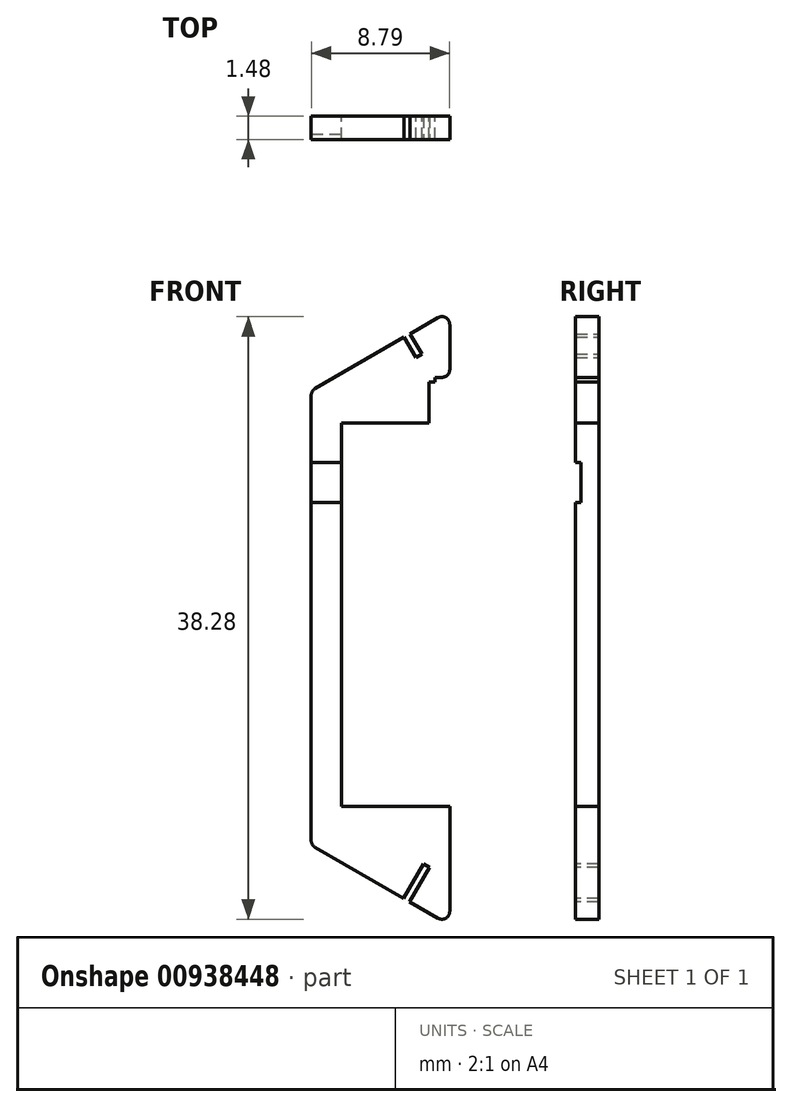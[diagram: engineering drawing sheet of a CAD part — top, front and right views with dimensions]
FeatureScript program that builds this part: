
annotation { "Feature Type Name" : "Feature", "Feature Type Description" : "" }
export const myFeature = defineFeature(function(context is Context, id is Id, definition is map)
    precondition{}
    {
        {
            var Q0;
            Q0=qCreatedBy(makeId("Front.planeOp"),FACE);
            var sketch = newSketch(context, id + "F0", { "sketchPlane" : qUnion([Q0])});
            skLineSegment(sketch, "E0", {"start": v(7.5, 30.48) * mm, "end": v(-1.3, 25.4) * mm});
            skLineSegment(sketch, "E1", {"start": v(-1.3, 25.4) * mm, "end": v(-1.3, -3.45) * mm});
            skLineSegment(sketch, "E2", {"start": v(-1.3, -3.45) * mm, "end": v(7.5, -8.53) * mm});
            skLineSegment(sketch, "E3", {"start": v(7.5, 30.48) * mm, "end": v(7.5, -8.53) * mm});
            skSolve(sketch);
        }
        {
            var Q0;
            Q0=makeQuery(id+"F0.imprint","IMPRINT",FACE,{"disambiguationData":[TD([[makeQuery(id+"F0.imprint","IMPRINT",EDGE,{"derivedFrom":sQuery(id+"F0.wireOp",EDGE,"E0")}),1.0]])]});
            extrude(context, id + "F1", {"entities" : qUnion([Q0]), "depth" : 16.18 * mm, "offsetDistance" : 25.4 * mm});
        }
        {
            var Q0;
            Q0=makeQuery(id+"F1.opExtrude","SWEPT_FACE",FACE,{"disambiguationData":[OSD([sQuery(id+"F0.wireOp",EDGE,"E3")])]});
            var sketch = newSketch(context, id + "F2", { "sketchPlane" : qUnion([Q0])});
            skLineSegment(sketch, "E4.bottom", {"start": v(-1.48, -8.53) * mm, "end": v(-16.18, -8.53) * mm});
            skLineSegment(sketch, "E4.top", {"start": v(-1.48, 30.48) * mm, "end": v(-16.18, 30.48) * mm});
            skLineSegment(sketch, "E4.left", {"start": v(-1.48, -8.53) * mm, "end": v(-1.48, 30.48) * mm});
            skLineSegment(sketch, "E4.right", {"start": v(-16.18, -8.53) * mm, "end": v(-16.18, 30.48) * mm});
            skSolve(sketch);
        }
        {
            var Q0;
            Q0=makeQuery(id+"F2.imprint","IMPRINT",FACE,{"disambiguationData":[TD([[makeQuery(id+"F2.imprint","IMPRINT",EDGE,{"derivedFrom":sQuery(id+"F2.wireOp",EDGE,"E4.bottom")}),1.0]])]});
            extrude(context, id + "F3", {"entities" : qUnion([Q0]), "operationType" : NewBodyOperationType.REMOVE, "oppositeDirection" : true, "depth" : 25.4 * mm, "offsetDistance" : 25.4 * mm});
        }
        {
            var Q0;
            Q0=makeQuery(id+"F0.imprint","IMPRINT",FACE,{"disambiguationData":[TD([[makeQuery(id+"F0.imprint","IMPRINT",EDGE,{"derivedFrom":sQuery(id+"F0.wireOp",EDGE,"E0")}),1.0]])]});
            var sketch = newSketch(context, id + "F4", { "sketchPlane" : qUnion([Q0])});
            skLineSegment(sketch, "E5.bottom", {"start": v(7.9, 23.36) * mm, "end": v(0.61, 23.36) * mm});
            skLineSegment(sketch, "E5.top", {"start": v(7.9, -1) * mm, "end": v(0.61, -1) * mm});
            skLineSegment(sketch, "E5.left", {"start": v(7.9, 23.36) * mm, "end": v(7.9, -1) * mm});
            skLineSegment(sketch, "E5.right", {"start": v(0.61, 23.36) * mm, "end": v(0.61, -1) * mm});
            skSolve(sketch);
        }
        {
            var Q0;
            Q0 = qSketchRegion(id + "F4", true);
            extrude(context, id + "F5", {"entities" : qUnion([Q0]), "operationType" : NewBodyOperationType.REMOVE, "depth" : 6.02 * mm, "offsetDistance" : 25.4 * mm});
        }
        {
            var Q0;
            Q0=makeQuery(id+"F1.opExtrude","SWEPT_FACE",FACE,{"disambiguationData":[OSD([sQuery(id+"F0.wireOp",EDGE,"E2")])]});
            var sketch = newSketch(context, id + "F6", { "sketchPlane" : qUnion([Q0])});
            skLineSegment(sketch, "E6.bottom", {"start": v(7.8, 0) * mm, "end": v(7.37, 0) * mm});
            skLineSegment(sketch, "E6.top", {"start": v(7.8, 1.48) * mm, "end": v(7.37, 1.48) * mm});
            skLineSegment(sketch, "E6.left", {"start": v(7.8, 0) * mm, "end": v(7.8, 1.48) * mm});
            skLineSegment(sketch, "E6.right", {"start": v(7.37, 0) * mm, "end": v(7.37, 1.48) * mm});
            skSolve(sketch);
        }
        {
            var Q0;
            Q0=makeQuery(id+"F6.imprint","IMPRINT",FACE,{"disambiguationData":[TD([[makeQuery(id+"F6.imprint","IMPRINT",EDGE,{"derivedFrom":sQuery(id+"F6.wireOp",EDGE,"E6.bottom")}),1.0]])]});
            extrude(context, id + "F7", {"entities" : qUnion([Q0]), "operationType" : NewBodyOperationType.REMOVE, "oppositeDirection" : true, "depth" : 2.54 * mm, "offsetDistance" : 25.4 * mm});
        }
        {
            var Q0;
            Q0=qCreatedBy(makeId("Front.planeOp"),FACE);
            var sketch = newSketch(context, id + "F8", { "sketchPlane" : qUnion([Q0])});
            skLineSegment(sketch, "E7.bottom", {"start": v(7.89, -0.86) * mm, "end": v(6.18, -0.86) * mm});
            skLineSegment(sketch, "E7.top", {"start": v(7.89, 25.98) * mm, "end": v(6.18, 25.98) * mm});
            skLineSegment(sketch, "E7.left", {"start": v(7.89, -0.86) * mm, "end": v(7.89, 25.98) * mm});
            skLineSegment(sketch, "E7.right", {"start": v(6.18, -0.86) * mm, "end": v(6.18, 25.98) * mm});
            skSolve(sketch);
        }
        {
            var Q0;
            Q0 = qSketchRegion(id + "F8", true);
            extrude(context, id + "F9", {"entities" : qUnion([Q0]), "operationType" : NewBodyOperationType.REMOVE, "depth" : 5.87 * mm, "offsetDistance" : 25.4 * mm});
        }
        {
            var Q0;
            Q0=qCreatedBy(makeId("Front.planeOp"),FACE);
            var sketch = newSketch(context, id + "F10", { "sketchPlane" : qUnion([Q0])});
            skLineSegment(sketch, "E8.bottom", {"start": v(6.55, 0.49) * mm, "end": v(10.86, 0.49) * mm});
            skLineSegment(sketch, "E8.top", {"start": v(6.55, 26.26) * mm, "end": v(10.86, 26.26) * mm});
            skLineSegment(sketch, "E8.left", {"start": v(6.55, 0.49) * mm, "end": v(6.55, 26.26) * mm});
            skLineSegment(sketch, "E8.right", {"start": v(10.86, 0.49) * mm, "end": v(10.86, 26.26) * mm});
            skSolve(sketch);
        }
        {
            var Q0;
            Q0=makeQuery(id+"F10.imprint","IMPRINT",FACE,{"disambiguationData":[TD([[makeQuery(id+"F10.imprint","IMPRINT",EDGE,{"derivedFrom":sQuery(id+"F10.wireOp",EDGE,"E8.bottom")}),1.0]])]});
            extrude(context, id + "F11", {"entities" : qUnion([Q0]), "operationType" : NewBodyOperationType.REMOVE, "depth" : 8.38 * mm, "offsetDistance" : 25.4 * mm});
        }
        {
            var Q0;
            Q0=makeQuery(id+"F1.opExtrude","SWEPT_FACE",FACE,{"disambiguationData":[OSD([sQuery(id+"F0.wireOp",EDGE,"E0")])]});
            var sketch = newSketch(context, id + "F12", { "sketchPlane" : qUnion([Q0])});
            skLineSegment(sketch, "E9.bottom", {"start": v(18.39, -1.48) * mm, "end": v(18.82, -1.48) * mm});
            skLineSegment(sketch, "E9.top", {"start": v(18.39, 0) * mm, "end": v(18.82, 0) * mm});
            skLineSegment(sketch, "E9.left", {"start": v(18.39, -1.48) * mm, "end": v(18.39, 0) * mm});
            skLineSegment(sketch, "E9.right", {"start": v(18.82, -1.48) * mm, "end": v(18.82, 0) * mm});
            skSolve(sketch);
        }
        {
            var Q0;
            Q0=makeQuery(id+"F12.imprint","IMPRINT",FACE,{"disambiguationData":[TD([[makeQuery(id+"F12.imprint","IMPRINT",EDGE,{"derivedFrom":sQuery(id+"F12.wireOp",EDGE,"E9.bottom")}),1.0]])]});
            extrude(context, id + "F13", {"entities" : qUnion([Q0]), "operationType" : NewBodyOperationType.REMOVE, "oppositeDirection" : true, "depth" : 1.5 * mm, "offsetDistance" : 25.4 * mm});
        }
        {
            var Q0;
            Q0=makeQuery(id+"F5.boolean.opBoolean","COPY",FACE,{"derivedFrom":makeQuery(id+"F5.opExtrude","SWEPT_FACE",FACE,{"disambiguationData":[OSD([sQuery(id+"F4.wireOp",EDGE,"E5.right")])]})});
            var sketch = newSketch(context, id + "F14", { "sketchPlane" : qUnion([Q0])});
            skLineSegment(sketch, "E10.bottom", {"start": v(-1.53, 20.84) * mm, "end": v(-1.14, 20.84) * mm});
            skLineSegment(sketch, "E10.top", {"start": v(-1.53, 18.3) * mm, "end": v(-1.14, 18.3) * mm});
            skLineSegment(sketch, "E10.left", {"start": v(-1.53, 20.84) * mm, "end": v(-1.53, 18.3) * mm});
            skLineSegment(sketch, "E10.right", {"start": v(-1.14, 20.84) * mm, "end": v(-1.14, 18.3) * mm});
            skSolve(sketch);
        }
        {
            var Q0;
            {var subQ0=sQuery(id+"F14.wireOp",EDGE,"E10.right");Q0=makeQuery(id+"F14.imprint","IMPRINT",FACE,{"disambiguationData":[TD([[makeQuery(id+"F14.imprint","IMPRINT",EDGE,{"derivedFrom":subQ0}),-1.0]])]});}
            var Q1;
            {var subQ0=sQuery(id+"F14.wireOp",EDGE,"E10.left");Q1=makeQuery(id+"F14.imprint","IMPRINT",FACE,{"disambiguationData":[TD([[makeQuery(id+"F14.imprint","IMPRINT",EDGE,{"derivedFrom":subQ0}),1.0]])]});}
            extrude(context, id + "F15", {"entities" : qUnion([Q0, Q1]), "operationType" : NewBodyOperationType.REMOVE, "oppositeDirection" : true, "depth" : 25.4 * mm, "offsetDistance" : 25.4 * mm});
        }
        {
            var Q0;
            Q0=makeQuery(id+"F1.opExtrude","SWEPT_EDGE",EDGE,{"disambiguationData":[OSD([sQuery(id+"F0.wireOp",EDGE,"E0"),sQuery(id+"F0.wireOp",EDGE,"E3")])]});
            var Q1;
            Q1=makeQuery(id+"F1.opExtrude","SWEPT_EDGE",EDGE,{"disambiguationData":[OSD([sQuery(id+"F0.wireOp",EDGE,"E2"),sQuery(id+"F0.wireOp",EDGE,"E3")])]});
            var Q2;
            Q2=makeQuery(id+"F1.opExtrude","SWEPT_EDGE",EDGE,{"disambiguationData":[OSD([sQuery(id+"F0.wireOp",EDGE,"E1"),sQuery(id+"F0.wireOp",EDGE,"E2")])]});
            var Q3;
            Q3=makeQuery(id+"F1.opExtrude","SWEPT_EDGE",EDGE,{"disambiguationData":[OSD([sQuery(id+"F0.wireOp",EDGE,"E0"),sQuery(id+"F0.wireOp",EDGE,"E1")])]});
            var Q4;
            {var subQ0=sQuery(id+"F0.wireOp",EDGE,"E0");var subQ1=sQuery(id+"F0.wireOp",EDGE,"E3");Q4=makeQuery(id+"F11.boolean.opBoolean","INTERSECT",EDGE,{"derivedFrom":[makeQuery(id+"F9.boolean.opBoolean","SPLIT",FACE,{"disambiguationData":[TD([makeQuery(id+"F1.opExtrude","SWEPT_FACE",FACE,{"disambiguationData":[OSD([subQ0])]})])],"derivedFrom":makeQuery(id+"F1.opExtrude","SWEPT_FACE",FACE,{"disambiguationData":[OSD([subQ1])]})}),makeQuery(id+"F11.opExtrude","SWEPT_FACE",FACE,{"disambiguationData":[OSD([sQuery(id+"F10.wireOp",EDGE,"E8.top")])]})]});}
            var Q5;
            Q5=makeQuery(id+"F9.boolean.opBoolean","INTERSECT",EDGE,{"derivedFrom":[makeQuery(id+"F1.opExtrude","SWEPT_FACE",FACE,{"disambiguationData":[OSD([sQuery(id+"F0.wireOp",EDGE,"E3")])]}),makeQuery(id+"F9.opExtrude","SWEPT_FACE",FACE,{"disambiguationData":[OSD([sQuery(id+"F8.wireOp",EDGE,"E7.bottom")])]})]});
            fillet(context, id + "F16", {"entities" : qUnion([Q0, Q1, Q2, Q3, Q4, Q5]), "radius" : .5 * mm, "tangentPropagation" : true, "allowEdgeOverflow" : false});
        }
    });
